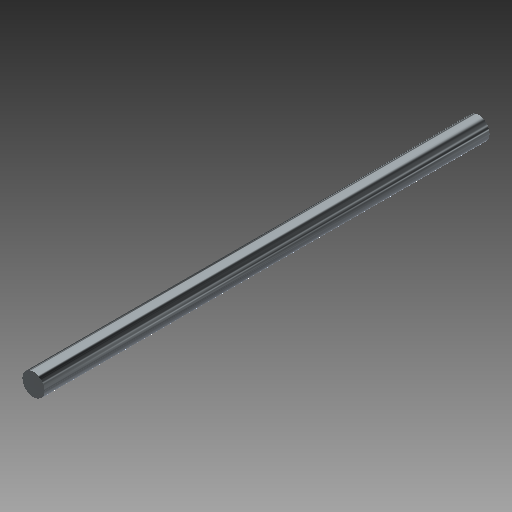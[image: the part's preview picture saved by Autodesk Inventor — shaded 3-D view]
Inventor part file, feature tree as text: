
AUTODESK INVENTOR PART (.ipt)
format: ipt  version: 2018 (Build 220112000, 112)  size: 94,720 bytes
history: native  units: in
note: dims shown in document units (in); Inventor stores cm internally (conversion verified against a paired STEP export)
features: extrude x1, sketch x1
ambient origin geometry x8: Origin, YZ Plane, XZ Plane, XY Plane, X Axis, Y Axis, Z Axis, Center Point
bodies: Solid1 (feature_tree)
feature tree (2):
  extrude  "Extrusion1"  Depth=2.5in TaperAngle=0.0deg
  sketch  "Sketch1"  dims[d0=0.125in d1=2.5in d2=0.0in]
